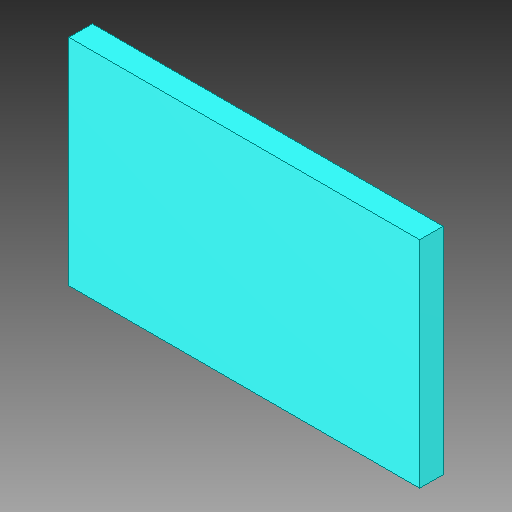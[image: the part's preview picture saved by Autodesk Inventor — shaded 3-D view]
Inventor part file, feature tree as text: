
AUTODESK INVENTOR PART (.ipt)
format: ipt  version: 2019 (Build 230136000, 136)  size: 85,504 bytes
history: native  units: in
note: dims shown in document units (in); Inventor stores cm internally (conversion verified against a paired STEP export)
features: extrude x1, other x1
ambient origin geometry x8: Origin, YZ Plane, XZ Plane, XY Plane, X Axis, Y Axis, Z Axis, Center Point
bodies: Solid1 (feature_tree)
feature tree (2):
  extrude  "Extrusion1"  Depth=0.0394in TaperAngle=0.0deg
  other  "W237-103, W237-103_27"
